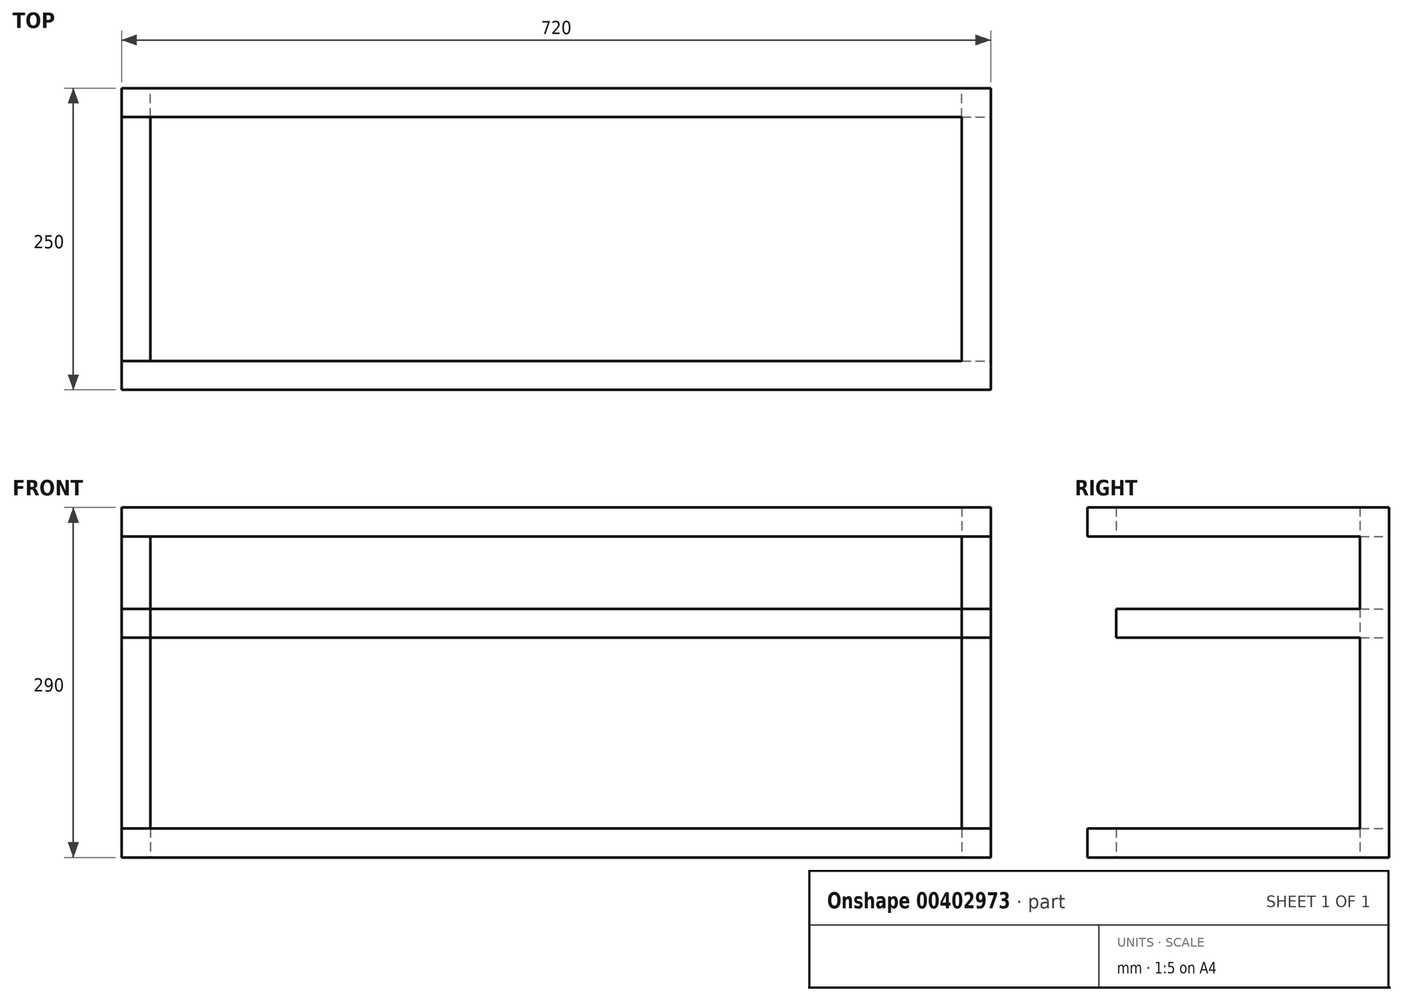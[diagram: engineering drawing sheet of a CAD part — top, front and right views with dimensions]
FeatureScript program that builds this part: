
annotation { "Feature Type Name" : "Feature", "Feature Type Description" : "" }
export const myFeature = defineFeature(function(context is Context, id is Id, definition is map)
    precondition{}
    {
        {
            var Q0;
            Q0=qCreatedBy(makeId("Front.planeOp"),FACE);
            var sketch = newSketch(context, id + "F0", { "sketchPlane" : qUnion([Q0])});
            skLineSegment(sketch, "E0.bottom", {"start": v(-354.03, 182.25) * mm, "end": v(365.97, 182.25) * mm});
            skLineSegment(sketch, "E0.top", {"start": v(-354.03, -107.75) * mm, "end": v(365.97, -107.75) * mm});
            skLineSegment(sketch, "E0.left", {"start": v(-354.03, 182.25) * mm, "end": v(-354.03, -107.75) * mm});
            skLineSegment(sketch, "E0.right", {"start": v(365.97, 182.25) * mm, "end": v(365.97, -107.75) * mm});
            skLineSegment(sketch, "E1", {"start": v(-354.03, -107.75) * mm, "end": v(-354.03, 86.25) * mm});
            skLineSegment(sketch, "E2.top", {"start": v(-354.03, 158.25) * mm, "end": v(365.97, 158.25) * mm});
            skLineSegment(sketch, "E2.left", {"start": v(-354.03, 182.25) * mm, "end": v(-354.03, 158.25) * mm});
            skLineSegment(sketch, "E2.right", {"start": v(365.97, 182.25) * mm, "end": v(365.97, 158.25) * mm});
            skLineSegment(sketch, "E3.bottom", {"start": v(365.97, 158.25) * mm, "end": v(341.97, 158.25) * mm});
            skLineSegment(sketch, "E3.left", {"start": v(365.97, 158.25) * mm, "end": v(365.97, 110.25) * mm});
            skLineSegment(sketch, "E4.bottom", {"start": v(-354.03, 158.25) * mm, "end": v(-330.03, 158.25) * mm});
            skLineSegment(sketch, "E4.left", {"start": v(-354.03, 158.25) * mm, "end": v(-354.03, 110.25) * mm});
            skLineSegment(sketch, "E5.top", {"start": v(-354.03, -83.75) * mm, "end": v(365.97, -83.75) * mm});
            skLineSegment(sketch, "E5.left", {"start": v(-354.03, -107.75) * mm, "end": v(-354.03, -83.75) * mm});
            skLineSegment(sketch, "E5.right", {"start": v(365.97, -107.75) * mm, "end": v(365.97, -83.75) * mm});
            skLineSegment(sketch, "E6.top", {"start": v(-354.03, -83.75) * mm, "end": v(-330.03, -83.75) * mm});
            skLineSegment(sketch, "E6.left", {"start": v(-354.03, 62.25) * mm, "end": v(-354.03, -83.75) * mm});
            skLineSegment(sketch, "E7.top", {"start": v(-354.03, 74.25) * mm, "end": v(365.97, 74.25) * mm});
            skLineSegment(sketch, "E7.right", {"start": v(365.97, 86.25) * mm, "end": v(365.97, 74.25) * mm});
            skLineSegment(sketch, "E8.top", {"start": v(-353.78, 98.25) * mm, "end": v(366.22, 98.25) * mm});
            skLineSegment(sketch, "E8.right", {"start": v(366.22, 86.25) * mm, "end": v(366.22, 98.25) * mm});
            skLineSegment(sketch, "E9.top", {"start": v(-353.78, 98.25) * mm, "end": v(-330.03, 98.25) * mm});
            skLineSegment(sketch, "E9.right", {"start": v(-330.03, 158.25) * mm, "end": v(-330.03, 98.25) * mm});
            skLineSegment(sketch, "E10", {"start": v(341.97, 158.25) * mm, "end": v(341.97, 98.25) * mm});
            skLineSegment(sketch, "E11", {"start": v(-330.03, -83.75) * mm, "end": v(-330.03, 74.25) * mm});
            skLineSegment(sketch, "E12", {"start": v(365.97, -83.75) * mm, "end": v(341.97, -83.75) * mm});
            skLineSegment(sketch, "E13", {"start": v(341.97, -83.75) * mm, "end": v(341.97, 74.25) * mm});
            skLineSegment(sketch, "E14", {"start": v(-354.03, 86.25) * mm, "end": v(365.97, 86.25) * mm});
            skSolve(sketch);
        }
        {
            var Q0;
            {var subQ1=sQuery(id+"F0.wireOp",EDGE,"E4.left");Q0=makeQuery(id+"F0.imprint","IMPRINT",FACE,{"disambiguationData":[TD([[makeQuery(id+"F0.imprint","IMPRINT",EDGE,{"derivedFrom":subQ1}),1.0]])]});}
            var Q1;
            Q1=makeQuery(id+"F0.imprint","IMPRINT",FACE,{"disambiguationData":[TD([[makeQuery(id+"F0.imprint","IMPRINT",EDGE,{"derivedFrom":sQuery(id+"F0.wireOp",EDGE,"E3.bottom")}),1.0]])]});
            var Q2;
            Q2=makeQuery(id+"F0.imprint","IMPRINT",FACE,{"disambiguationData":[TD([[makeQuery(id+"F0.imprint","IMPRINT",EDGE,{"derivedFrom":sQuery(id+"F0.wireOp",EDGE,"E6.top")}),1.0]])]});
            var Q3;
            {var subQ0=sQuery(id+"F0.wireOp",EDGE,"E12");Q3=makeQuery(id+"F0.imprint","IMPRINT",FACE,{"disambiguationData":[TD([[makeQuery(id+"F0.imprint","IMPRINT",EDGE,{"derivedFrom":subQ0}),-1.0]])]});}
            var Q4;
            {var subQ0=sQuery(id+"F0.wireOp",EDGE,"E7.right");Q4=makeQuery(id+"F0.imprint","IMPRINT",FACE,{"disambiguationData":[TD([[makeQuery(id+"F0.imprint","IMPRINT",EDGE,{"derivedFrom":subQ0}),-1.0]])]});}
            var Q5;
            {var subQ0=sQuery(id+"F0.wireOp",EDGE,"E8.right");Q5=makeQuery(id+"F0.imprint","IMPRINT",FACE,{"disambiguationData":[TD([[makeQuery(id+"F0.imprint","IMPRINT",EDGE,{"derivedFrom":subQ0}),1.0]])]});}
            var Q6;
            Q6=makeQuery(id+"F0.imprint","IMPRINT",FACE,{"disambiguationData":[TD([[makeQuery(id+"F0.imprint","IMPRINT",EDGE,{"derivedFrom":sQuery(id+"F0.wireOp",EDGE,"E0.bottom")}),-1.0]])]});
            var Q7;
            Q7=makeQuery(id+"F0.imprint","IMPRINT",FACE,{"disambiguationData":[TD([[makeQuery(id+"F0.imprint","IMPRINT",EDGE,{"derivedFrom":sQuery(id+"F0.wireOp",EDGE,"E0.top")}),1.0]])]});
            extrude(context, id + "F1", {"entities" : qUnion([Q0, Q1, Q2, Q3, Q4, Q5, Q6, Q7]), "oppositeDirection" : true, "depth" : 24 * mm});
        }
        {
            var Q0;
            Q0=makeQuery(id+"F1.opExtrude","CAP_FACE",FACE,{"disambiguationData":[OSD([sQuery(id+"F0.wireOp",EDGE,"E0.left"),sQuery(id+"F0.wireOp",EDGE,"E0.right"),sQuery(id+"F0.wireOp",EDGE,"E1"),sQuery(id+"F0.wireOp",EDGE,"E0.bottom"),sQuery(id+"F0.wireOp",EDGE,"E2.top"),sQuery(id+"F0.wireOp",EDGE,"E2.left"),sQuery(id+"F0.wireOp",EDGE,"E2.right"),sQuery(id+"F0.wireOp",EDGE,"E3.left"),sQuery(id+"F0.wireOp",EDGE,"E4.bottom"),sQuery(id+"F0.wireOp",EDGE,"E4.left"),sQuery(id+"F0.wireOp",EDGE,"E0.top"),sQuery(id+"F0.wireOp",EDGE,"E5.top"),sQuery(id+"F0.wireOp",EDGE,"E5.left"),sQuery(id+"F0.wireOp",EDGE,"E5.right"),sQuery(id+"F0.wireOp",EDGE,"E6.left"),sQuery(id+"F0.wireOp",EDGE,"E7.top"),sQuery(id+"F0.wireOp",EDGE,"E7.right"),sQuery(id+"F0.wireOp",EDGE,"E8.top"),sQuery(id+"F0.wireOp",EDGE,"E8.right"),sQuery(id+"F0.wireOp",EDGE,"E9.right"),sQuery(id+"F0.wireOp",EDGE,"E10"),sQuery(id+"F0.wireOp",EDGE,"E11"),sQuery(id+"F0.wireOp",EDGE,"E13")])],"isStart":false});
            var sketch = newSketch(context, id + "F2", { "sketchPlane" : qUnion([Q0])});
            skLineSegment(sketch, "E15.bottom", {"start": v(-365.97, 182.25) * mm, "end": v(-341.97, 182.25) * mm});
            skLineSegment(sketch, "E15.top", {"start": v(-365.97, 158.25) * mm, "end": v(-341.97, 158.25) * mm});
            skLineSegment(sketch, "E15.left", {"start": v(-365.97, 182.25) * mm, "end": v(-365.97, 158.25) * mm});
            skLineSegment(sketch, "E15.right", {"start": v(-341.97, 182.25) * mm, "end": v(-341.97, 158.25) * mm});
            skLineSegment(sketch, "E16.bottom", {"start": v(-341.97, 98.25) * mm, "end": v(-365.97, 98.25) * mm});
            skLineSegment(sketch, "E16.top", {"start": v(-341.97, 74.25) * mm, "end": v(-365.97, 74.25) * mm});
            skLineSegment(sketch, "E16.left", {"start": v(-341.97, 98.25) * mm, "end": v(-341.97, 74.25) * mm});
            skLineSegment(sketch, "E16.right", {"start": v(-365.97, 98.25) * mm, "end": v(-365.97, 74.25) * mm});
            skLineSegment(sketch, "E17.bottom", {"start": v(-341.97, -83.75) * mm, "end": v(-365.97, -83.75) * mm});
            skLineSegment(sketch, "E17.top", {"start": v(-341.97, -107.75) * mm, "end": v(-365.97, -107.75) * mm});
            skLineSegment(sketch, "E17.left", {"start": v(-341.97, -83.75) * mm, "end": v(-341.97, -107.75) * mm});
            skLineSegment(sketch, "E17.right", {"start": v(-365.97, -83.75) * mm, "end": v(-365.97, -107.75) * mm});
            skLineSegment(sketch, "E18.bottom", {"start": v(330.03, 158.25) * mm, "end": v(354.03, 158.25) * mm});
            skLineSegment(sketch, "E18.top", {"start": v(330.03, 182.25) * mm, "end": v(354.03, 182.25) * mm});
            skLineSegment(sketch, "E18.left", {"start": v(330.03, 158.25) * mm, "end": v(330.03, 182.25) * mm});
            skLineSegment(sketch, "E18.right", {"start": v(354.03, 158.25) * mm, "end": v(354.03, 182.25) * mm});
            skLineSegment(sketch, "E19.bottom", {"start": v(330.03, 98.25) * mm, "end": v(354.03, 98.25) * mm});
            skLineSegment(sketch, "E19.top", {"start": v(330.03, 74.25) * mm, "end": v(354.03, 74.25) * mm});
            skLineSegment(sketch, "E19.left", {"start": v(330.03, 98.25) * mm, "end": v(330.03, 74.25) * mm});
            skLineSegment(sketch, "E19.right", {"start": v(354.03, 98.25) * mm, "end": v(354.03, 74.25) * mm});
            skLineSegment(sketch, "E20.bottom", {"start": v(330.03, -83.75) * mm, "end": v(354.03, -83.75) * mm});
            skLineSegment(sketch, "E20.top", {"start": v(330.03, -107.75) * mm, "end": v(354.03, -107.75) * mm});
            skLineSegment(sketch, "E20.left", {"start": v(330.03, -83.75) * mm, "end": v(330.03, -107.75) * mm});
            skLineSegment(sketch, "E20.right", {"start": v(354.03, -83.75) * mm, "end": v(354.03, -107.75) * mm});
            skSolve(sketch);
        }
        {
            var Q0;
            Q0=makeQuery(id+"F2.imprint","IMPRINT",FACE,{"disambiguationData":[TD([[makeQuery(id+"F2.imprint","IMPRINT",EDGE,{"derivedFrom":sQuery(id+"F2.wireOp",EDGE,"E16.bottom")}),1.0]])]});
            var Q1;
            Q1=makeQuery(id+"F2.imprint","IMPRINT",FACE,{"disambiguationData":[TD([[makeQuery(id+"F2.imprint","IMPRINT",EDGE,{"derivedFrom":sQuery(id+"F2.wireOp",EDGE,"E17.bottom")}),1.0]])]});
            var Q2;
            Q2=makeQuery(id+"F2.imprint","IMPRINT",FACE,{"disambiguationData":[TD([[makeQuery(id+"F2.imprint","IMPRINT",EDGE,{"derivedFrom":sQuery(id+"F2.wireOp",EDGE,"E18.bottom")}),1.0]])]});
            var Q3;
            Q3=makeQuery(id+"F2.imprint","IMPRINT",FACE,{"disambiguationData":[TD([[makeQuery(id+"F2.imprint","IMPRINT",EDGE,{"derivedFrom":sQuery(id+"F2.wireOp",EDGE,"E20.bottom")}),-1.0]])]});
            var Q4;
            Q4=makeQuery(id+"F2.imprint","IMPRINT",FACE,{"disambiguationData":[TD([[makeQuery(id+"F2.imprint","IMPRINT",EDGE,{"derivedFrom":sQuery(id+"F2.wireOp",EDGE,"E19.bottom")}),-1.0]])]});
            var Q5;
            Q5=makeQuery(id+"F2.imprint","IMPRINT",FACE,{"disambiguationData":[TD([[makeQuery(id+"F2.imprint","IMPRINT",EDGE,{"derivedFrom":sQuery(id+"F2.wireOp",EDGE,"E15.bottom")}),1.0]])]});
            extrude(context, id + "F3", {"entities" : qUnion([Q0, Q1, Q2, Q3, Q4, Q5]), "operationType" : NewBodyOperationType.ADD, "depth" : 202 * mm});
        }
        {
            var Q0;
            Q0=makeQuery(id+"F3.boolean.opBoolean","MERGE",FACE,{"derivedFrom":[makeQuery(id+"F1.opExtrude","SWEPT_FACE",FACE,{"disambiguationData":[OSD([sQuery(id+"F0.wireOp",EDGE,"E0.right"),sQuery(id+"F0.wireOp",EDGE,"E2.right"),sQuery(id+"F0.wireOp",EDGE,"E3.left"),sQuery(id+"F0.wireOp",EDGE,"E5.right"),sQuery(id+"F0.wireOp",EDGE,"E7.right")])]}),makeQuery(id+"F3.opExtrude","SWEPT_FACE",FACE,{"disambiguationData":[OSD([sQuery(id+"F2.wireOp",EDGE,"E15.left")])]}),makeQuery(id+"F3.opExtrude","SWEPT_FACE",FACE,{"disambiguationData":[OSD([sQuery(id+"F2.wireOp",EDGE,"E16.right")])]}),makeQuery(id+"F3.opExtrude","SWEPT_FACE",FACE,{"disambiguationData":[OSD([sQuery(id+"F2.wireOp",EDGE,"E17.right")])]})]});
            var sketch = newSketch(context, id + "F4", { "sketchPlane" : qUnion([Q0])});
            skLineSegment(sketch, "E21.bottom", {"start": v(226, 182.25) * mm, "end": v(250, 182.25) * mm});
            skLineSegment(sketch, "E21.top", {"start": v(226, 158.25) * mm, "end": v(250, 158.25) * mm});
            skLineSegment(sketch, "E21.left", {"start": v(226, 182.25) * mm, "end": v(226, 158.25) * mm});
            skLineSegment(sketch, "E21.right", {"start": v(250, 182.25) * mm, "end": v(250, 158.25) * mm});
            skLineSegment(sketch, "E22.bottom", {"start": v(226, 98.25) * mm, "end": v(250, 98.25) * mm});
            skLineSegment(sketch, "E22.top", {"start": v(226, 74.25) * mm, "end": v(250, 74.25) * mm});
            skLineSegment(sketch, "E22.left", {"start": v(226, 98.25) * mm, "end": v(226, 74.25) * mm});
            skLineSegment(sketch, "E22.right", {"start": v(250, 98.25) * mm, "end": v(250, 74.25) * mm});
            skLineSegment(sketch, "E23.bottom", {"start": v(226, -83.75) * mm, "end": v(250, -83.75) * mm});
            skLineSegment(sketch, "E23.top", {"start": v(226, -107.75) * mm, "end": v(250, -107.75) * mm});
            skLineSegment(sketch, "E23.left", {"start": v(226, -83.75) * mm, "end": v(226, -107.75) * mm});
            skLineSegment(sketch, "E23.right", {"start": v(250, -83.75) * mm, "end": v(250, -107.75) * mm});
            skSolve(sketch);
        }
        {
            var Q0;
            Q0=makeQuery(id+"F4.imprint","IMPRINT",FACE,{"disambiguationData":[TD([[makeQuery(id+"F4.imprint","IMPRINT",EDGE,{"derivedFrom":sQuery(id+"F4.wireOp",EDGE,"E22.bottom")}),-1.0]])]});
            var Q1;
            Q1=makeQuery(id+"F4.imprint","IMPRINT",FACE,{"disambiguationData":[TD([[makeQuery(id+"F4.imprint","IMPRINT",EDGE,{"derivedFrom":sQuery(id+"F4.wireOp",EDGE,"E21.bottom")}),-1.0]])]});
            var Q2;
            Q2=makeQuery(id+"F4.imprint","IMPRINT",FACE,{"disambiguationData":[TD([[makeQuery(id+"F4.imprint","IMPRINT",EDGE,{"derivedFrom":sQuery(id+"F4.wireOp",EDGE,"E23.bottom")}),-1.0]])]});
            extrude(context, id + "F5", {"entities" : qUnion([Q0, Q1, Q2]), "operationType" : NewBodyOperationType.ADD, "oppositeDirection" : true, "depth" : 720 * mm});
        }
        {
            var Q0;
            Q0=makeQuery(id+"F5.boolean.opBoolean","MERGE",FACE,{"derivedFrom":[makeQuery(id+"F3.boolean.opBoolean","MERGE",FACE,{"derivedFrom":[makeQuery(id+"F1.opExtrude","SWEPT_FACE",FACE,{"disambiguationData":[OSD([sQuery(id+"F0.wireOp",EDGE,"E0.bottom")])]}),makeQuery(id+"F3.opExtrude","SWEPT_FACE",FACE,{"disambiguationData":[OSD([sQuery(id+"F2.wireOp",EDGE,"E15.bottom")])]}),makeQuery(id+"F3.opExtrude","SWEPT_FACE",FACE,{"disambiguationData":[OSD([sQuery(id+"F2.wireOp",EDGE,"E18.top")])]})]}),makeQuery(id+"F5.opExtrude","SWEPT_FACE",FACE,{"disambiguationData":[OSD([sQuery(id+"F4.wireOp",EDGE,"E21.bottom")])]})]});
            var sketch = newSketch(context, id + "F6", { "sketchPlane" : qUnion([Q0])});
            skLineSegment(sketch, "E24.bottom", {"start": v(-354.03, 250) * mm, "end": v(-330.03, 250) * mm});
            skLineSegment(sketch, "E24.top", {"start": v(-354.03, 226) * mm, "end": v(-330.03, 226) * mm});
            skLineSegment(sketch, "E24.left", {"start": v(-354.03, 250) * mm, "end": v(-354.03, 226) * mm});
            skLineSegment(sketch, "E24.right", {"start": v(-330.03, 250) * mm, "end": v(-330.03, 226) * mm});
            skLineSegment(sketch, "E25.bottom", {"start": v(365.97, 250) * mm, "end": v(341.97, 250) * mm});
            skLineSegment(sketch, "E25.top", {"start": v(365.97, 226) * mm, "end": v(341.97, 226) * mm});
            skLineSegment(sketch, "E25.left", {"start": v(365.97, 250) * mm, "end": v(365.97, 226) * mm});
            skLineSegment(sketch, "E25.right", {"start": v(341.97, 250) * mm, "end": v(341.97, 226) * mm});
            skSolve(sketch);
        }
        {
            var Q0;
            Q0 = qSketchRegion(id + "F6", true);
            extrude(context, id + "F7", {"entities" : qUnion([Q0]), "operationType" : NewBodyOperationType.ADD, "oppositeDirection" : true, "depth" : 280 * mm});
        }
    });
